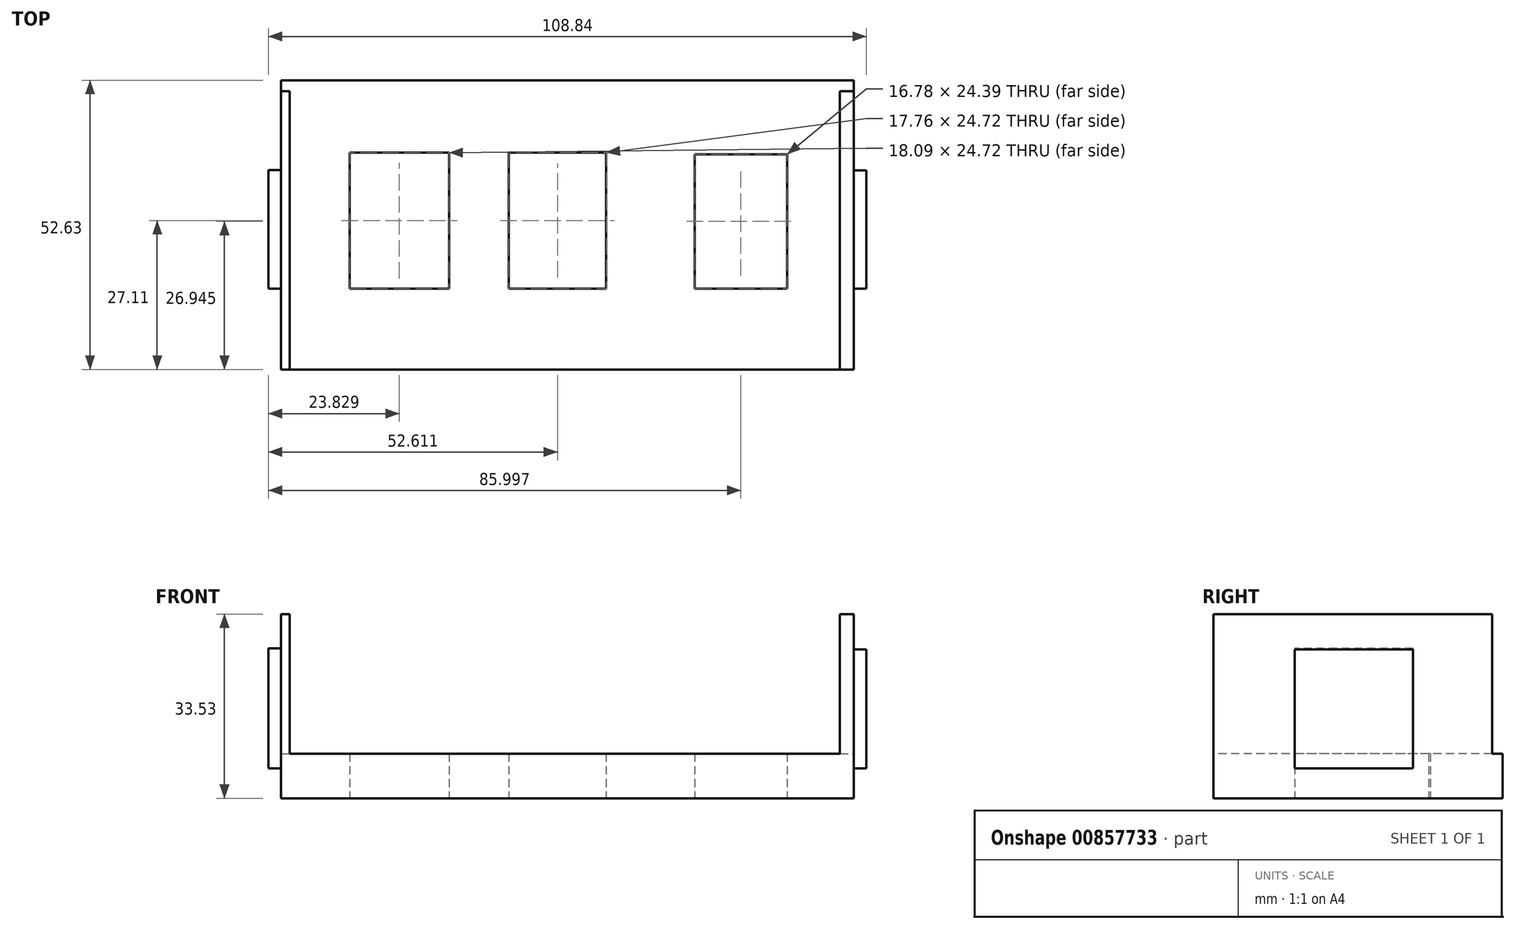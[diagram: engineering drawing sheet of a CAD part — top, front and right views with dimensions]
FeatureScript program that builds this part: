
annotation { "Feature Type Name" : "Feature", "Feature Type Description" : "" }
export const myFeature = defineFeature(function(context is Context, id is Id, definition is map)
    precondition{}
    {
        {
            var Q0;
            Q0=qCreatedBy(makeId("Top.planeOp"),FACE);
            var sketch = newSketch(context, id + "F0", { "sketchPlane" : qUnion([Q0])});
            skLineSegment(sketch, "E0.bottom", {"start": v(-48.12, 37.88) * mm, "end": v(56.15, 37.88) * mm});
            skLineSegment(sketch, "E0.top", {"start": v(-48.12, -14.75) * mm, "end": v(56.15, -14.75) * mm});
            skLineSegment(sketch, "E0.left", {"start": v(-48.12, 37.88) * mm, "end": v(-48.12, -14.75) * mm});
            skLineSegment(sketch, "E0.right", {"start": v(56.15, 37.88) * mm, "end": v(56.15, -14.75) * mm});
            skLineSegment(sketch, "E1.bottom", {"start": v(-35.62, 24.72) * mm, "end": v(-17.53, 24.72) * mm});
            skLineSegment(sketch, "E1.top", {"start": v(-35.62, 0) * mm, "end": v(-17.53, 0) * mm});
            skLineSegment(sketch, "E1.left", {"start": v(-35.62, 24.72) * mm, "end": v(-35.62, 0) * mm});
            skLineSegment(sketch, "E1.right", {"start": v(-17.53, 24.72) * mm, "end": v(-17.53, 0) * mm});
            skLineSegment(sketch, "E2.bottom", {"start": v(-6.67, 24.72) * mm, "end": v(11.1, 24.72) * mm});
            skLineSegment(sketch, "E2.top", {"start": v(-6.67, 0) * mm, "end": v(11.1, 0) * mm});
            skLineSegment(sketch, "E2.left", {"start": v(-6.67, 24.72) * mm, "end": v(-6.67, 0) * mm});
            skLineSegment(sketch, "E2.right", {"start": v(11.1, 24.72) * mm, "end": v(11.1, 0) * mm});
            skLineSegment(sketch, "E3.bottom", {"start": v(27.2, 24.4) * mm, "end": v(43.98, 24.4) * mm});
            skLineSegment(sketch, "E3.top", {"start": v(27.2, 0) * mm, "end": v(43.98, 0) * mm});
            skLineSegment(sketch, "E3.left", {"start": v(27.2, 24.4) * mm, "end": v(27.2, 0) * mm});
            skLineSegment(sketch, "E3.right", {"start": v(43.98, 24.4) * mm, "end": v(43.98, 0) * mm});
            skSolve(sketch);
        }
        {
            var Q0;
            Q0=makeQuery(id+"F0.imprint","IMPRINT",FACE,{"disambiguationData":[TD([[makeQuery(id+"F0.imprint","IMPRINT",EDGE,{"derivedFrom":sQuery(id+"F0.wireOp",EDGE,"E0.bottom")}),-1.0]])]});
            extrude(context, id + "F1", {"entities" : qUnion([Q0]), "depth" : 8.13 * mm, "offsetDistance" : 25.4 * mm});
        }
        {
            var Q0;
            Q0=makeQuery(id+"F1.opExtrude","CAP_FACE",FACE,{"disambiguationData":[OSD([sQuery(id+"F0.wireOp",EDGE,"E0.bottom"),sQuery(id+"F0.wireOp",EDGE,"E0.top"),sQuery(id+"F0.wireOp",EDGE,"E0.left"),sQuery(id+"F0.wireOp",EDGE,"E0.right"),sQuery(id+"F0.wireOp",EDGE,"E1.bottom"),sQuery(id+"F0.wireOp",EDGE,"E1.top"),sQuery(id+"F0.wireOp",EDGE,"E1.left"),sQuery(id+"F0.wireOp",EDGE,"E1.right"),sQuery(id+"F0.wireOp",EDGE,"E2.bottom"),sQuery(id+"F0.wireOp",EDGE,"E2.top"),sQuery(id+"F0.wireOp",EDGE,"E2.left"),sQuery(id+"F0.wireOp",EDGE,"E2.right"),sQuery(id+"F0.wireOp",EDGE,"E3.bottom"),sQuery(id+"F0.wireOp",EDGE,"E3.top"),sQuery(id+"F0.wireOp",EDGE,"E3.left"),sQuery(id+"F0.wireOp",EDGE,"E3.right")])],"isStart":false});
            var sketch = newSketch(context, id + "F2", { "sketchPlane" : qUnion([Q0])});
            skLineSegment(sketch, "E4.bottom", {"start": v(-48.12, 37.88) * mm, "end": v(-46.56, 37.88) * mm});
            skLineSegment(sketch, "E4.top", {"start": v(-48.12, -14.75) * mm, "end": v(-46.56, -14.75) * mm});
            skLineSegment(sketch, "E4.left", {"start": v(-48.12, 37.88) * mm, "end": v(-48.12, -14.75) * mm});
            skLineSegment(sketch, "E4.right", {"start": v(-46.56, 37.88) * mm, "end": v(-46.56, -14.75) * mm});
            skLineSegment(sketch, "E5.bottom", {"start": v(-48.12, 37.88) * mm, "end": v(56.15, 37.88) * mm});
            skLineSegment(sketch, "E5.top", {"start": v(-48.12, 35.93) * mm, "end": v(56.15, 35.93) * mm});
            skLineSegment(sketch, "E5.left", {"start": v(-48.12, 37.88) * mm, "end": v(-48.12, 35.93) * mm});
            skLineSegment(sketch, "E5.right", {"start": v(56.15, 37.88) * mm, "end": v(56.15, 35.93) * mm});
            skLineSegment(sketch, "E6.bottom", {"start": v(56.15, 37.88) * mm, "end": v(53.61, 37.88) * mm});
            skLineSegment(sketch, "E6.top", {"start": v(56.15, -14.75) * mm, "end": v(53.61, -14.75) * mm});
            skLineSegment(sketch, "E6.left", {"start": v(56.15, 37.88) * mm, "end": v(56.15, -14.75) * mm});
            skLineSegment(sketch, "E6.right", {"start": v(53.61, 37.88) * mm, "end": v(53.61, -14.75) * mm});
            skSolve(sketch);
        }
        {
            var Q0;
            {var subQ0=sQuery(id+"F2.wireOp",EDGE,"E4.top");Q0=makeQuery(id+"F2.imprint","IMPRINT",FACE,{"disambiguationData":[TD([[makeQuery(id+"F2.imprint","IMPRINT",EDGE,{"derivedFrom":subQ0}),1.0]])]});}
            var Q1;
            {var subQ5=sQuery(id+"F2.wireOp",EDGE,"E6.top");Q1=makeQuery(id+"F2.imprint","IMPRINT",FACE,{"disambiguationData":[TD([[makeQuery(id+"F2.imprint","IMPRINT",EDGE,{"derivedFrom":subQ5}),1.0]])]});}
            extrude(context, id + "F3", {"entities" : qUnion([Q0, Q1]), "operationType" : NewBodyOperationType.ADD, "depth" : 25.4 * mm, "offsetDistance" : 25.4 * mm});
        }
        {
            var Q0;
            Q0=makeQuery(id+"F3.boolean.opBoolean","MERGE",FACE,{"derivedFrom":[makeQuery(id+"F1.opExtrude","SWEPT_FACE",FACE,{"disambiguationData":[OSD([sQuery(id+"F0.wireOp",EDGE,"E0.right")])]}),makeQuery(id+"F3.opExtrude","SWEPT_FACE",FACE,{"disambiguationData":[OSD([sQuery(id+"F2.wireOp",EDGE,"E6.left")])]})]});
            var sketch = newSketch(context, id + "F4", { "sketchPlane" : qUnion([Q0])});
            skLineSegment(sketch, "E7.bottom", {"start": v(0, 27.1) * mm, "end": v(21.51, 27.1) * mm});
            skLineSegment(sketch, "E7.top", {"start": v(0, 5.47) * mm, "end": v(21.51, 5.47) * mm});
            skLineSegment(sketch, "E7.left", {"start": v(0, 27.1) * mm, "end": v(0, 5.47) * mm});
            skLineSegment(sketch, "E7.right", {"start": v(21.51, 27.1) * mm, "end": v(21.51, 5.47) * mm});
            skSolve(sketch);
        }
        {
            var Q0;
            Q0=makeQuery(id+"F3.boolean.opBoolean","MERGE",FACE,{"derivedFrom":[makeQuery(id+"F1.opExtrude","SWEPT_FACE",FACE,{"disambiguationData":[OSD([sQuery(id+"F0.wireOp",EDGE,"E0.left")])]}),makeQuery(id+"F3.opExtrude","SWEPT_FACE",FACE,{"disambiguationData":[OSD([sQuery(id+"F2.wireOp",EDGE,"E4.left")])]})]});
            var sketch = newSketch(context, id + "F5", { "sketchPlane" : qUnion([Q0])});
            skLineSegment(sketch, "E8.bottom", {"start": v(-21.54, 27.26) * mm, "end": v(0, 27.26) * mm});
            skLineSegment(sketch, "E8.top", {"start": v(-21.54, 5.4) * mm, "end": v(0, 5.4) * mm});
            skLineSegment(sketch, "E8.left", {"start": v(-21.54, 27.26) * mm, "end": v(-21.54, 5.4) * mm});
            skLineSegment(sketch, "E8.right", {"start": v(0, 27.26) * mm, "end": v(0, 5.4) * mm});
            skSolve(sketch);
        }
        {
            var Q0;
            Q0=makeQuery(id+"F4.imprint","IMPRINT",FACE,{"disambiguationData":[TD([[makeQuery(id+"F4.imprint","IMPRINT",EDGE,{"derivedFrom":sQuery(id+"F4.wireOp",EDGE,"E7.bottom")}),-1.0]])]});
            extrude(context, id + "F6", {"entities" : qUnion([Q0]), "operationType" : NewBodyOperationType.ADD, "depth" : 2.3 * mm, "offsetDistance" : 25.4 * mm});
        }
        {
            var Q0;
            Q0=makeQuery(id+"F5.imprint","IMPRINT",FACE,{"disambiguationData":[TD([[makeQuery(id+"F5.imprint","IMPRINT",EDGE,{"derivedFrom":sQuery(id+"F5.wireOp",EDGE,"E8.bottom")}),-1.0]])]});
            extrude(context, id + "F7", {"entities" : qUnion([Q0]), "operationType" : NewBodyOperationType.ADD, "depth" : 2.3 * mm, "offsetDistance" : 25.4 * mm});
        }
    });
